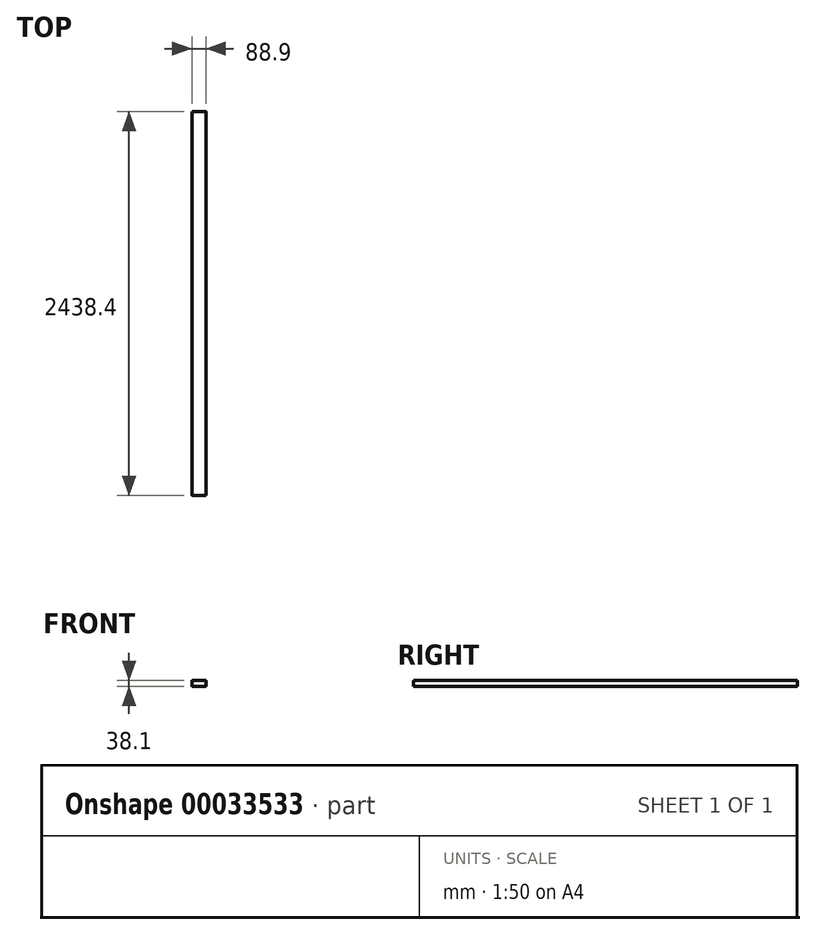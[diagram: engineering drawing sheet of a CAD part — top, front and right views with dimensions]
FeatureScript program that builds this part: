
annotation { "Feature Type Name" : "Feature", "Feature Type Description" : "" }
export const myFeature = defineFeature(function(context is Context, id is Id, definition is map)
    precondition{}
    {
        {
            var Q0;
            Q0=qCreatedBy(makeId("Front.planeOp"),FACE);
            var sketch = newSketch(context, id + "F0", { "sketchPlane" : qUnion([Q0])});
            skLineSegment(sketch, "E0.rect.bottom", {"start": v(41.28, 19.05) * mm, "end": v(-41.28, 19.05) * mm});
            skLineSegment(sketch, "E0.rect.top", {"start": v(41.28, -19.05) * mm, "end": v(-41.27, -19.05) * mm});
            skLineSegment(sketch, "E0.rect.left", {"start": v(44.45, 15.88) * mm, "end": v(44.45, -15.88) * mm});
            skLineSegment(sketch, "E0.rect.right", {"start": v(-44.45, 15.88) * mm, "end": v(-44.45, -15.88) * mm});
            skPoint(sketch, "E0.rect.middle", {"position": v(0, 0) * mm});
            skPoint(sketch, "E1.visualSharp", {"position": v(-44.45, 19.05) * mm});
            skArc(sketch, "E1.filletArc", {"start": v(-41.28, 19.05) * mm, "mid": v(-43.52, 18.12) * mm, "end": v(-44.45, 15.88) * mm});
            skPoint(sketch, "E2.visualSharp", {"position": v(44.45, 19.05) * mm});
            skArc(sketch, "E2.filletArc", {"start": v(44.45, 15.88) * mm, "mid": v(43.52, 18.12) * mm, "end": v(41.28, 19.05) * mm});
            skPoint(sketch, "E3.visualSharp", {"position": v(44.45, -19.05) * mm});
            skArc(sketch, "E3.filletArc", {"start": v(41.28, -19.05) * mm, "mid": v(43.52, -18.12) * mm, "end": v(44.45, -15.88) * mm});
            skPoint(sketch, "E4.visualSharp", {"position": v(-44.45, -19.05) * mm});
            skArc(sketch, "E4.filletArc", {"start": v(-44.45, -15.88) * mm, "mid": v(-43.52, -18.12) * mm, "end": v(-41.27, -19.05) * mm});
            skSolve(sketch);
        }
        {
            var Q0;
            Q0=makeQuery(id+"F0.imprint","IMPRINT",FACE,{"disambiguationData":[TD([[makeQuery(id+"F0.imprint","IMPRINT",EDGE,{"derivedFrom":sQuery(id+"F0.wireOp",EDGE,"E0.rect.bottom")}),1.0]])]});
            extrude(context, id + "F1", {"entities" : qUnion([Q0]), "oppositeDirection" : true, "depth" : 2438.4 * mm});
        }
    });
